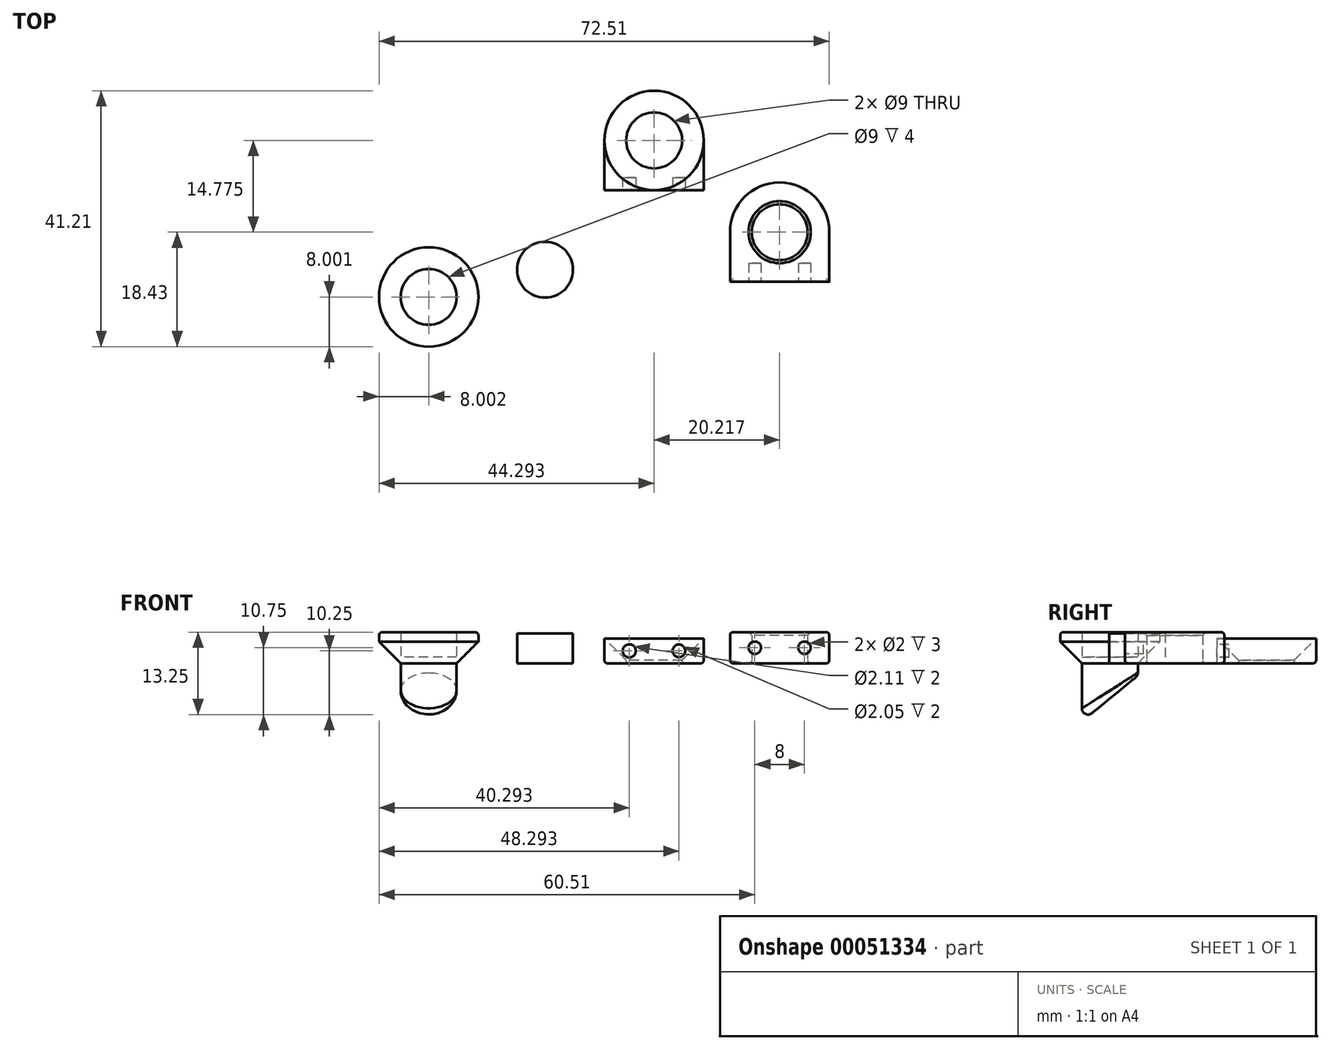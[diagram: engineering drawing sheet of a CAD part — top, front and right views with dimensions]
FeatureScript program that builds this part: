
annotation { "Feature Type Name" : "Feature", "Feature Type Description" : "" }
export const myFeature = defineFeature(function(context is Context, id is Id, definition is map)
    precondition{}
    {
        {
            var Q0;
            Q0=qCreatedBy(makeId("Top.planeOp"),FACE);
            var sketch = newSketch(context, id + "F0", { "sketchPlane" : qUnion([Q0])});
            skCircle(sketch, "E0", {"center": v(0, 0) * mm, "radius": 4.5 * mm});
            skArc(sketch, "E1", {"start": v(8, 0) * mm, "mid": v(0, 8) * mm, "end": v(-8, 0) * mm});
            skLineSegment(sketch, "E2", {"start": v(-8, 0) * mm, "end": v(-8, -8) * mm});
            skLineSegment(sketch, "E3", {"start": v(8, 0) * mm, "end": v(8, -8) * mm});
            skLineSegment(sketch, "E4", {"start": v(-8, -8) * mm, "end": v(8, -8) * mm});
            skCircle(sketch, "E5", {"center": v(-20.22, 14.78) * mm, "radius": 4.5 * mm});
            skArc(sketch, "E6", {"start": v(-12.22, 14.78) * mm, "mid": v(-20.22, 22.78) * mm, "end": v(-28.22, 14.78) * mm});
            skLineSegment(sketch, "E7", {"start": v(-28.22, 14.78) * mm, "end": v(-28.22, 6.78) * mm});
            skLineSegment(sketch, "E8", {"start": v(-12.22, 14.78) * mm, "end": v(-12.22, 6.78) * mm});
            skLineSegment(sketch, "E9", {"start": v(-28.22, 6.78) * mm, "end": v(-12.22, 6.78) * mm});
            skCircle(sketch, "E10", {"center": v(-37.78, -6.05) * mm, "radius": 4.5 * mm});
            skCircle(sketch, "E11", {"center": v(-56.5, -10.43) * mm, "radius": 4.5 * mm});
            skCircle(sketch, "E12", {"center": v(-56.5, -10.43) * mm, "radius": 8 * mm});
            skSolve(sketch);
        }
        {
            var Q0;
            Q0=makeQuery(id+"F0.imprint","IMPRINT",FACE,{"disambiguationData":[TD([[makeQuery(id+"F0.imprint","IMPRINT",EDGE,{"derivedFrom":sQuery(id+"F0.wireOp",EDGE,"E10")}),1.0]])]});
            extrude(context, id + "F1", {"entities" : qUnion([Q0]), "depth" : 4.8 * mm});
        }
        {
            var Q0;
            Q0=makeQuery(id+"F0.imprint","IMPRINT",FACE,{"disambiguationData":[TD([[makeQuery(id+"F0.imprint","IMPRINT",EDGE,{"derivedFrom":sQuery(id+"F0.wireOp",EDGE,"E0")}),-1.0]])]});
            extrude(context, id + "F2", {"entities" : qUnion([Q0]), "depth" : 5 * mm});
        }
        {
            var Q0;
            Q0=makeQuery(id+"F0.imprint","IMPRINT",FACE,{"disambiguationData":[TD([[makeQuery(id+"F0.imprint","IMPRINT",EDGE,{"derivedFrom":sQuery(id+"F0.wireOp",EDGE,"E5")}),-1.0]])]});
            extrude(context, id + "F3", {"entities" : qUnion([Q0]), "depth" : 4 * mm});
        }
        {
            var Q0;
            Q0=makeQuery(id+"F3.opExtrude","CAP_EDGE",EDGE,{"disambiguationData":[OSD([sQuery(id+"F0.wireOp",EDGE,"E5")])],"isStart":false});
            chamfer(context, id + "F4", {"entities" : qUnion([Q0]), "width" : 3.5 * mm, "tangentPropagation" : true});
        }
        {
            var Q0;
            Q0=makeQuery(id+"F0.imprint","IMPRINT",FACE,{"disambiguationData":[TD([[makeQuery(id+"F0.imprint","IMPRINT",EDGE,{"derivedFrom":sQuery(id+"F0.wireOp",EDGE,"E11")}),-1.0]])]});
            extrude(context, id + "F5", {"entities" : qUnion([Q0]), "depth" : 5 * mm});
        }
        {
            var Q0;
            Q0=makeQuery(id+"F0.imprint","IMPRINT",FACE,{"disambiguationData":[TD([[makeQuery(id+"F0.imprint","IMPRINT",EDGE,{"derivedFrom":sQuery(id+"F0.wireOp",EDGE,"E11")}),1.0]])]});
            extrude(context, id + "F6", {"entities" : qUnion([Q0]), "operationType" : NewBodyOperationType.ADD, "oppositeDirection" : true, "depth" : 10 * mm});
        }
        {
            var Q0;
            Q0=makeQuery(id+"F0.imprint","IMPRINT",FACE,{"disambiguationData":[TD([[makeQuery(id+"F0.imprint","IMPRINT",EDGE,{"derivedFrom":sQuery(id+"F0.wireOp",EDGE,"E11")}),1.0]])]});
            extrude(context, id + "F7", {"entities" : qUnion([Q0]), "operationType" : NewBodyOperationType.ADD, "depth" : 1 * mm});
        }
        {
            var Q0;
            Q0=makeQuery(id+"F5.opExtrude","CAP_EDGE",EDGE,{"disambiguationData":[OSD([sQuery(id+"F0.wireOp",EDGE,"E12")])],"isStart":true});
            chamfer(context, id + "F8", {"entities" : qUnion([Q0]), "width" : 3.5 * mm, "tangentPropagation" : true});
        }
        {
            var Q0;
            Q0=makeQuery(id+"F2.opExtrude","SWEPT_FACE",FACE,{"disambiguationData":[OSD([sQuery(id+"F0.wireOp",EDGE,"E4")])]});
            var sketch = newSketch(context, id + "F9", { "sketchPlane" : qUnion([Q0])});
            skLineSegment(sketch, "E13", {"start": v(4, 5) * mm, "end": v(8, 5) * mm});
            skLineSegment(sketch, "E14", {"start": v(8, 5) * mm, "end": v(8, 0) * mm});
            skLineSegment(sketch, "E15", {"start": v(-8, 2.5) * mm, "end": v(-8, 5) * mm});
            skCircle(sketch, "E16", {"center": v(-4, 2.5) * mm, "radius": 1 * mm});
            skCircle(sketch, "E17", {"center": v(4, 2.5) * mm, "radius": 1 * mm});
            skPoint(sketch, "E18.orphan", {"position": v(-4, 5) * mm});
            skPoint(sketch, "E19.orphan", {"position": v(-8, 2.5) * mm});
            skPoint(sketch, "E20.orphan", {"position": v(-4, 0) * mm});
            skPoint(sketch, "E21.orphan", {"position": v(4, 0) * mm});
            skPoint(sketch, "E22.orphan", {"position": v(8, 2.5) * mm});
            skSolve(sketch);
        }
        {
            var Q0;
            Q0=makeQuery(id+"F9.imprint","IMPRINT",FACE,{"disambiguationData":[TD([[makeQuery(id+"F9.imprint","IMPRINT",EDGE,{"derivedFrom":sQuery(id+"F9.wireOp",EDGE,"E16")}),1.0]])]});
            var Q1;
            Q1=makeQuery(id+"F9.imprint","IMPRINT",FACE,{"disambiguationData":[TD([[makeQuery(id+"F9.imprint","IMPRINT",EDGE,{"derivedFrom":sQuery(id+"F9.wireOp",EDGE,"E17")}),1.0]])]});
            extrude(context, id + "F10", {"entities" : qUnion([Q0, Q1]), "operationType" : NewBodyOperationType.REMOVE, "oppositeDirection" : true, "depth" : 3 * mm});
        }
        {
            var Q0;
            Q0=makeQuery(id+"F3.opExtrude","SWEPT_FACE",FACE,{"disambiguationData":[OSD([sQuery(id+"F0.wireOp",EDGE,"E9")])]});
            var sketch = newSketch(context, id + "F11", { "sketchPlane" : qUnion([Q0])});
            skCircle(sketch, "E23", {"center": v(-24.22, 2) * mm, "radius": 1.06 * mm});
            skCircle(sketch, "E24", {"center": v(-16.22, 2) * mm, "radius": 1.02 * mm});
            skPoint(sketch, "E25.orphan", {"position": v(-20.22, 0) * mm});
            skPoint(sketch, "E26.end.orphan", {"position": v(-20.22, 2) * mm});
            skPoint(sketch, "E26.start.orphan", {"position": v(-20.22, 4) * mm});
            skSolve(sketch);
        }
        {
            var Q0;
            Q0=makeQuery(id+"F11.imprint","IMPRINT",FACE,{"disambiguationData":[TD([[makeQuery(id+"F11.imprint","IMPRINT",EDGE,{"derivedFrom":sQuery(id+"F11.wireOp",EDGE,"E24")}),1.0]])]});
            var Q1;
            Q1=makeQuery(id+"F11.imprint","IMPRINT",FACE,{"disambiguationData":[TD([[makeQuery(id+"F11.imprint","IMPRINT",EDGE,{"derivedFrom":sQuery(id+"F11.wireOp",EDGE,"E23")}),1.0]])]});
            extrude(context, id + "F12", {"entities" : qUnion([Q0, Q1]), "operationType" : NewBodyOperationType.REMOVE, "oppositeDirection" : true, "depth" : 2 * mm});
        }
        {
            var Q0;
            Q0=qCreatedBy(makeId("Right.planeOp"),FACE);
            var sketch = newSketch(context, id + "F13", { "sketchPlane" : qUnion([Q0])});
            skLineSegment(sketch, "E27", {"start": v(-5.84, -5.2) * mm, "end": v(-5.84, -7) * mm});
            skLineSegment(sketch, "E28", {"start": v(-5.84, -7) * mm, "end": v(-5.84, -8.37) * mm});
            skLineSegment(sketch, "E29", {"start": v(-5.84, -5.2) * mm, "end": v(-5.84, -3.42) * mm});
            skLineSegment(sketch, "E30", {"start": v(-5.84, -3.42) * mm, "end": v(-5.84, -1.9) * mm});
            skLineSegment(sketch, "E31", {"start": v(-16.53, -10.67) * mm, "end": v(-5.84, -10.67) * mm});
            skLineSegment(sketch, "E32", {"start": v(-5.84, -10.67) * mm, "end": v(-5.84, -8.37) * mm});
            skLineSegment(sketch, "E33", {"start": v(-5.84, -1.9) * mm, "end": v(-16.53, -10.67) * mm});
            skSolve(sketch);
        }
        {
            var Q0;
            Q0=makeQuery(id+"F13.imprint","IMPRINT",FACE,{"disambiguationData":[TD([[makeQuery(id+"F13.imprint","IMPRINT",EDGE,{"derivedFrom":sQuery(id+"F13.wireOp",EDGE,"E27")}),-1.0]])]});
            extrude(context, id + "F14", {"entities" : qUnion([Q0]), "operationType" : NewBodyOperationType.REMOVE, "endBound" : BoundingType.THROUGH_ALL, "oppositeDirection" : true, "depth" : 25 * mm});
        }
        {
            var Q0;
            Q0=makeQuery(id+"F2.opExtrude","CAP_EDGE",EDGE,{"disambiguationData":[OSD([sQuery(id+"F0.wireOp",EDGE,"E0")])],"isStart":false});
            chamfer(context, id + "F15", {"entities" : qUnion([Q0]), "width" : .5 * mm, "tangentPropagation" : true});
        }
        {
            var Q0;
            Q0=makeQuery(id+"F14.boolean.opBoolean","COPY",FACE,{"derivedFrom":makeQuery(id+"F14.opExtrude","SWEPT_FACE",FACE,{"disambiguationData":[OSD([sQuery(id+"F13.wireOp",EDGE,"E33")])]})});
            var Q1;
            {var subQ0=sQuery(id+"F0.wireOp",EDGE,"E11");Q1=makeQuery(id+"F14.boolean.opBoolean","INTERSECT",EDGE,{"derivedFrom":[makeQuery(id+"F7.boolean.opBoolean","MERGE",FACE,{"derivedFrom":[makeQuery(id+"F6.opExtrude","SWEPT_FACE",FACE,{"disambiguationData":[OSD([subQ0])]}),makeQuery(id+"F7.opExtrude","SWEPT_FACE",FACE,{"disambiguationData":[OSD([subQ0])]})]}),makeQuery(id+"F14.opExtrude","SWEPT_FACE",FACE,{"disambiguationData":[OSD([sQuery(id+"F13.wireOp",EDGE,"E33")])]})]});}
            fillet(context, id + "F16", {"entities" : qUnion([Q0, Q1]), "radius" : 1 * mm, "tangentPropagation" : true, "allowEdgeOverflow" : false});
        }
        {
            var Q0;
            Q0=makeQuery(id+"F2.opExtrude","CAP_FACE",FACE,{"disambiguationData":[OSD([sQuery(id+"F0.wireOp",EDGE,"E0"),sQuery(id+"F0.wireOp",EDGE,"E1"),sQuery(id+"F0.wireOp",EDGE,"E2"),sQuery(id+"F0.wireOp",EDGE,"E3"),sQuery(id+"F0.wireOp",EDGE,"E4")])],"isStart":true});
            var Q1;
            Q1=makeQuery(id+"F2.opExtrude","CAP_EDGE",EDGE,{"disambiguationData":[OSD([sQuery(id+"F0.wireOp",EDGE,"E3")])],"isStart":false});
            var Q2;
            Q2=makeQuery(id+"F5.opExtrude","CAP_EDGE",EDGE,{"disambiguationData":[OSD([sQuery(id+"F0.wireOp",EDGE,"E12")])],"isStart":false});
            var Q3;
            Q3=makeQuery(id+"F3.opExtrude","CAP_EDGE",EDGE,{"disambiguationData":[OSD([sQuery(id+"F0.wireOp",EDGE,"E8")])],"isStart":true});
            var Q4;
            Q4=makeQuery(id+"F3.opExtrude","CAP_EDGE",EDGE,{"disambiguationData":[OSD([sQuery(id+"F0.wireOp",EDGE,"E6")])],"isStart":true});
            var Q5;
            Q5=makeQuery(id+"F3.opExtrude","CAP_EDGE",EDGE,{"disambiguationData":[OSD([sQuery(id+"F0.wireOp",EDGE,"E7")])],"isStart":true});
            fillet(context, id + "F17", {"entities" : qUnion([Q0, Q1, Q2, Q3, Q4, Q5]), "radius" : .5 * mm, "tangentPropagation" : true, "allowEdgeOverflow" : false});
        }
    });
